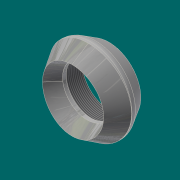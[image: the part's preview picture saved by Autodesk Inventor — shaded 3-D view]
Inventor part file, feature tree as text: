
AUTODESK INVENTOR PART (.ipt)
format: ipt  version: 2017.3 (Build 213257000, 257)  size: 370,688 bytes
history: native  units: mm (DEFAULTED — no unit token found)
features: other x8, sketch x5, plane x1, extrude x1, revolve x1, thread x1, sweep x1
ambient origin geometry x8: Origin, YZ Plane, XZ Plane, XY Plane, X Axis, Y Axis, Z Axis, Center Point
bodies: Solid1 (feature_tree)
feature tree (18):
  sketch  "Sketch1"  dims[d5=38.1mm d8=90.0deg]
  plane  "Work Plane1"
  sketch  "Sketch2"  dims[d9=0.0mm d10=917.575mm d11=10.0mm d12=0.0mm]
  extrude  "Extrusion1"  TaperAngle=90.0deg  [1 undecoded]
  revolve  "Revolution2"  [1 undecoded]
  thread  "Thread1"  [1 undecoded]
  other  "Work Point1"
  sweep  "Sweep1"
  other  "Work Axis3"
  other  "Work Point2"
  other  "Work Point3"
  sketch  "Sketch3"  dims[d45=8.810625mm d52=88.10625mm]
  sketch  "Sketch4"  dims[d54=1185.06875mm d77=68.1482mm d80=38.1mm d81=19.2151mm d83=56.55818mm d85=0.312398mm d86=90.0deg d91=52.5018mm d92=6.0mm d93=4.0mm d94=2.0mm d95=90.0deg d96=3.84302mm d97=0.0mm d102=10.0mm d103=0.0mm d106=19.05mm d107=496.8875mm d120=-458.7875mm d121=0.0mm d129=0.78232mm d130=0.78232mm d131=30.0deg d132=11.509375mm d133=0.0mm d134=0.0mm d135=90.0deg d136=0.0mm d137=90.0deg d138=65.0875mm d139=58.3692mm d140=0.0mm]
  other  "Work Axis2"
  sketch  "3D Sketch1"
  other  "Edges14"
  other  "Edges15"
  other  "Work Axis4"
note: 3 required parameter values undecoded (feature->parameter linkage not recoverable at this tier; creation-order binding heuristic only, values carry confidence <= 0.55)